# Revit family: ROBUST-xxx-8xx-Tx
name_source: partatom
category: Oprawy oświetleniowe
revit_build: Autodesk Revit 2017 (Build: 20190508_0315(x64)
units: mm (PartAtom-declared; Revit-internal decimal feet)

## family parameters
Numer OmniClass = 23.80.70.11
Obiekt nadrzędny = Powierzchnia
Punkt obliczania pomieszczeń = Nie
Tnij formami wycięć po wczytaniu = Nie
Typ części = Normalny
Tytuł OmniClass = Luminaries for Internal Lighting
Współdzielony = Nie
Wymiar okrągłego złącza = Użyj średnicy
Źródło światła = Tak

## types (8) — shared parameters
Emituj kształt widoczny w renderingu = Nie
Emituj z długości prostokąta = 386 mm  [stored 1.2664 ft]
Emituj z szerokości prostokąta = 293 mm
Filtr koloru = 16777215
Kod zespołu = D5020200
Lampa = LED
Odchylenie kierunku = 90.00°
Plik sieci fotometrycznej = ROBUST 15000-840 T.IES
Producent = RIDI Leuchten GmbH
URL = www.ridi.de
Zmiana temperatury barwowej przyciemniania lampy = <Brak>
brand = RIDI
conformity mark = CE
electrical safety class = 1
height = 92 mm  [stored 0.301837 ft]
ingress protection (IP) code = IP20
length = 425 mm  [stored 1.39436 ft]
nominal frequency = 50-60Hz
nominal voltage = 230
voltage type (AC, DC, UC) = AC
weight = 8.8 kg
width = 414 mm  [stored 1.35827 ft]
zero-valued in all types: Domyślna rzędna

## per-type parameters (varying)
| type | Model | Obciążenie pozorne | rated input power |
| ROBUST 15000-840 T-DA | 0660577 | 113 VA | 113 |
| ROBUST 15000-865 T | 0650648 | 113 VA | 113 |
| ROBUST 23000-840 T | 0650578 | 170 VA | 170 |
| ROBUST 23000-840 T-DA | 0660578 | 170 VA | 170 |
| ROBUST 23000-865 T | 0650649 | 170 VA | 170 |
| ROBUST 23000-865 T-DA | 0660649 | 170 VA | 170 |
| ROBUST 15000-840 T | 0650577 | 113 VA | 113 |
| ROBUST 15000-865 T-DA | 0660648 | 113 VA | 113 |

note: column(s) folded — value = type name in every type: product name

note: [stored X ft] marks values corroborated as IEEE doubles in the binary element streams (Revit-internal decimal feet)
